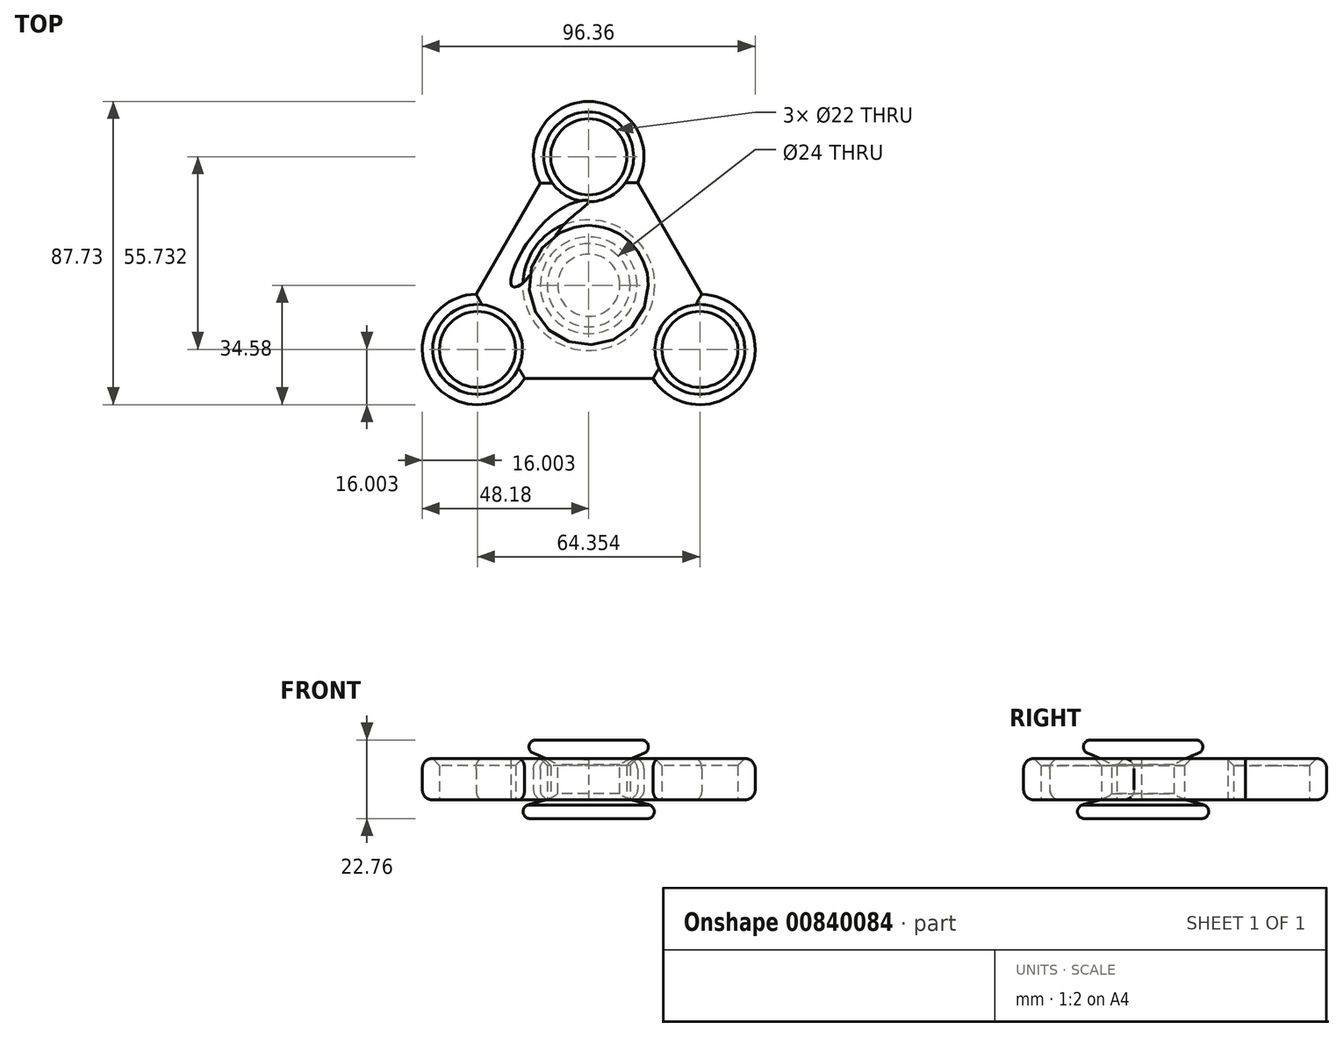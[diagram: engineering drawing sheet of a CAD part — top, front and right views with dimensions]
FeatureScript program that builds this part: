
annotation { "Feature Type Name" : "Feature", "Feature Type Description" : "" }
export const myFeature = defineFeature(function(context is Context, id is Id, definition is map)
    precondition{}
    {
        {
            var Q0;
            Q0=qCreatedBy(makeId("Top.planeOp"),FACE);
            var sketch = newSketch(context, id + "F0", { "sketchPlane" : qUnion([Q0])});
            skCircle(sketch, "E0", {"center": v(0, 37.15) * mm, "radius": 11 * mm});
            skArc(sketch, "E1.0", {"start": v(14.07, 29.53) * mm, "mid": v(0, 53.15) * mm, "end": v(-14.07, 29.53) * mm});
            skArc(sketch, "E2.1.0", {"start": v(-32.61, -2.58) * mm, "mid": v(-46.03, -26.58) * mm, "end": v(-18.54, -26.95) * mm});
            skCircle(sketch, "E2.1.1", {"center": v(-32.18, -18.58) * mm, "radius": 11 * mm});
            skArc(sketch, "E2.2.0", {"start": v(18.54, -26.95) * mm, "mid": v(46.03, -26.58) * mm, "end": v(32.61, -2.58) * mm});
            skCircle(sketch, "E2.2.1", {"center": v(32.18, -18.58) * mm, "radius": 11 * mm});
            skPoint(sketch, "E2.center", {"position": v(0, 0) * mm});
            skCircle(sketch, "E3", {"center": v(0, 0) * mm, "radius": 12 * mm});
            skPoint(sketch, "E4.0.midPoint", {"position": v(-32.71, 0) * mm});
            skArc(sketch, "E5.trimOffspring", {"start": v(18.42, -27.04) * mm, "mid": v(18.48, -27) * mm, "end": v(18.54, -26.95) * mm, "construction": true});
            skPoint(sketch, "E6.orphan", {"position": v(-32.71, -18.89) * mm});
            skPoint(sketch, "E7.orphan", {"position": v(0, 37.77) * mm});
            skArc(sketch, "E8.trimOffspring", {"start": v(14.2, 29.47) * mm, "mid": v(14.14, 29.5) * mm, "end": v(14.07, 29.53) * mm, "construction": true});
            skArc(sketch, "E9.trimOffspring", {"start": v(32.61, -2.58) * mm, "mid": v(32.62, -2.5) * mm, "end": v(32.62, -2.43) * mm, "construction": true});
            skPoint(sketch, "E10.orphan", {"position": v(32.71, -18.89) * mm});
            skPoint(sketch, "E11.visualSharp", {"position": v(-32.71, 18.89) * mm});
            skPoint(sketch, "E12.visualSharp", {"position": v(32.71, 18.89) * mm});
            skPoint(sketch, "E13.visualSharp", {"position": v(0, -37.77) * mm});
            skLineSegment(sketch, "E14", {"start": v(14.12, 29.62) * mm, "end": v(32.71, -2.59) * mm});
            skLineSegment(sketch, "E15", {"start": v(-14.07, 29.53) * mm, "end": v(-32.61, -2.58) * mm});
            skLineSegment(sketch, "E16", {"start": v(-18.54, -26.95) * mm, "end": v(18.6, -27.04) * mm});
            skSolve(sketch);
        }
        {
            var Q0;
            Q0=makeQuery(id+"F0.imprint","IMPRINT",FACE,{"disambiguationData":[TD([[makeQuery(id+"F0.imprint","IMPRINT",EDGE,{"derivedFrom":sQuery(id+"F0.wireOp",EDGE,"E0")}),-1.0]])]});
            extrude(context, id + "F1", {"entities" : qUnion([Q0]), "endBound" : BoundingType.SYMMETRIC, "depth" : 12 * mm, "offsetDistance" : 25 * mm});
        }
        {
            var Q0;
            Q0=makeQuery(id+"F1.opExtrude","CAP_EDGE",EDGE,{"disambiguationData":[OSD([sQuery(id+"F0.wireOp",EDGE,"E4.1")])],"isStart":false});
            var Q1;
            Q1=makeQuery(id+"F1.opExtrude","CAP_EDGE",EDGE,{"disambiguationData":[OSD([sQuery(id+"F0.wireOp",EDGE,"E11.filletArc")])],"isStart":false});
            var Q2;
            Q2=makeQuery(id+"F1.opExtrude","CAP_EDGE",EDGE,{"disambiguationData":[OSD([sQuery(id+"F0.wireOp",EDGE,"E4.0")])],"isStart":false});
            var Q3;
            Q3=makeQuery(id+"F1.opExtrude","CAP_EDGE",EDGE,{"disambiguationData":[OSD([sQuery(id+"F0.wireOp",EDGE,"E2.1.0")])],"isStart":false});
            var Q4;
            Q4=makeQuery(id+"F1.opExtrude","CAP_EDGE",EDGE,{"disambiguationData":[OSD([sQuery(id+"F0.wireOp",EDGE,"E4.5")])],"isStart":false});
            var Q5;
            Q5=makeQuery(id+"F1.opExtrude","CAP_EDGE",EDGE,{"disambiguationData":[OSD([sQuery(id+"F0.wireOp",EDGE,"E4.4")])],"isStart":false});
            var Q6;
            Q6=makeQuery(id+"F1.opExtrude","CAP_EDGE",EDGE,{"disambiguationData":[OSD([sQuery(id+"F0.wireOp",EDGE,"E13.filletArc")])],"isStart":false});
            var Q7;
            Q7=makeQuery(id+"F1.opExtrude","CAP_EDGE",EDGE,{"disambiguationData":[OSD([sQuery(id+"F0.wireOp",EDGE,"E2.2.0")])],"isStart":false});
            var Q8;
            Q8=makeQuery(id+"F1.opExtrude","CAP_EDGE",EDGE,{"disambiguationData":[OSD([sQuery(id+"F0.wireOp",EDGE,"E4.3")])],"isStart":false});
            var Q9;
            Q9=makeQuery(id+"F1.opExtrude","CAP_EDGE",EDGE,{"disambiguationData":[OSD([sQuery(id+"F0.wireOp",EDGE,"E12.filletArc")])],"isStart":false});
            var Q10;
            Q10=makeQuery(id+"F1.opExtrude","CAP_EDGE",EDGE,{"disambiguationData":[OSD([sQuery(id+"F0.wireOp",EDGE,"E4.2")])],"isStart":false});
            var Q11;
            Q11=makeQuery(id+"F1.opExtrude","CAP_EDGE",EDGE,{"disambiguationData":[OSD([sQuery(id+"F0.wireOp",EDGE,"E1.0")])],"isStart":false});
            fillet(context, id + "F2", {"entities" : qUnion([Q0, Q1, Q2, Q3, Q4, Q5, Q6, Q7, Q8, Q9, Q10, Q11]), "radius" : 3 * mm, "tangentPropagation" : true, "allowEdgeOverflow" : false});
        }
        {
            var Q0;
            Q0=makeQuery(id+"F1.opExtrude","CAP_FACE",FACE,{"disambiguationData":[OSD([sQuery(id+"F0.wireOp",EDGE,"E0"),sQuery(id+"F0.wireOp",EDGE,"E1.0"),sQuery(id+"F0.wireOp",EDGE,"E2.1.0"),sQuery(id+"F0.wireOp",EDGE,"E2.1.1"),sQuery(id+"F0.wireOp",EDGE,"E2.2.0"),sQuery(id+"F0.wireOp",EDGE,"E2.2.1"),sQuery(id+"F0.wireOp",EDGE,"E3"),sQuery(id+"F0.wireOp",EDGE,"E4.0"),sQuery(id+"F0.wireOp",EDGE,"E4.1"),sQuery(id+"F0.wireOp",EDGE,"E4.2"),sQuery(id+"F0.wireOp",EDGE,"E4.3"),sQuery(id+"F0.wireOp",EDGE,"E4.4"),sQuery(id+"F0.wireOp",EDGE,"E4.5"),sQuery(id+"F0.wireOp",EDGE,"E11.filletArc"),sQuery(id+"F0.wireOp",EDGE,"E12.filletArc"),sQuery(id+"F0.wireOp",EDGE,"E13.filletArc")])],"isStart":false});
            var sketch = newSketch(context, id + "F3", { "sketchPlane" : qUnion([Q0])});
            skPoint(sketch, "E17.0.internal.snap0", {"position": v(-18.02, 22.93) * mm});
            skPoint(sketch, "E17.7.internal.snap0", {"position": v(-18.02, 24.33) * mm});
            skFitSpline(sketch, "E17", {"points": [v(-6.56, 22.93) * mm, v(-15.86, 14.71) * mm, v(-20.62, 7.32) * mm, v(-22.39, 0) * mm, v(-19.88, 0) * mm, v(-11.64, 11.2) * mm, v(-5.23, 19.44) * mm, v(0, 24.33) * mm, v(-6.56, 22.93) * mm]});
            skSolve(sketch);
        }
        {
            var Q0;
            Q0=makeQuery(id+"F3.imprint","IMPRINT",FACE,{"disambiguationData":[TD([[makeQuery(id+"F3.imprint","IMPRINT",EDGE,{"derivedFrom":sQuery(id+"F3.wireOp",EDGE,"E17")}),1.0]])]});
            extrude(context, id + "F4", {"entities" : qUnion([Q0]), "operationType" : NewBodyOperationType.REMOVE, "endBound" : BoundingType.THROUGH_ALL, "oppositeDirection" : true, "depth" : 7 * mm, "offsetDistance" : 25 * mm});
        }
        {
            var Q0;
            Q0=makeQuery(id+"F1.opExtrude","CAP_EDGE",EDGE,{"disambiguationData":[OSD([sQuery(id+"F0.wireOp",EDGE,"E15")])],"isStart":false});
            var Q1;
            Q1=makeQuery(id+"F1.opExtrude","CAP_EDGE",EDGE,{"disambiguationData":[OSD([sQuery(id+"F0.wireOp",EDGE,"E16")])],"isStart":false});
            var Q2;
            Q2=makeQuery(id+"F1.opExtrude","CAP_EDGE",EDGE,{"disambiguationData":[OSD([sQuery(id+"F0.wireOp",EDGE,"E14")])],"isStart":false});
            fillet(context, id + "F5", {"entities" : qUnion([Q0, Q1, Q2]), "radius" : 3 * mm, "tangentPropagation" : true, "allowEdgeOverflow" : false});
        }
        {
            var Q0;
            Q0=makeQuery(id+"F1.opExtrude","CAP_EDGE",EDGE,{"disambiguationData":[OSD([sQuery(id+"F0.wireOp",EDGE,"E15")])],"isStart":true});
            var Q1;
            Q1=makeQuery(id+"F1.opExtrude","CAP_EDGE",EDGE,{"disambiguationData":[OSD([sQuery(id+"F0.wireOp",EDGE,"E2.1.0")])],"isStart":true});
            var Q2;
            Q2=makeQuery(id+"F1.opExtrude","CAP_EDGE",EDGE,{"disambiguationData":[OSD([sQuery(id+"F0.wireOp",EDGE,"E16")])],"isStart":true});
            var Q3;
            Q3=makeQuery(id+"F1.opExtrude","CAP_EDGE",EDGE,{"disambiguationData":[OSD([sQuery(id+"F0.wireOp",EDGE,"E2.2.0")])],"isStart":true});
            var Q4;
            Q4=makeQuery(id+"F1.opExtrude","CAP_EDGE",EDGE,{"disambiguationData":[OSD([sQuery(id+"F0.wireOp",EDGE,"E14")])],"isStart":true});
            var Q5;
            Q5=makeQuery(id+"F1.opExtrude","CAP_EDGE",EDGE,{"disambiguationData":[OSD([sQuery(id+"F0.wireOp",EDGE,"E1.0")])],"isStart":true});
            fillet(context, id + "F6", {"entities" : qUnion([Q0, Q1, Q2, Q3, Q4, Q5]), "radius" : 3 * mm, "tangentPropagation" : true, "allowEdgeOverflow" : false});
        }
        {
            var Q0;
            Q0=makeQuery(id+"F1.opExtrude","CAP_EDGE",EDGE,{"disambiguationData":[OSD([sQuery(id+"F0.wireOp",EDGE,"E3")])],"isStart":false});
            var Q1;
            Q1=makeQuery(id+"F1.opExtrude","CAP_EDGE",EDGE,{"disambiguationData":[OSD([sQuery(id+"F0.wireOp",EDGE,"E2.2.1")])],"isStart":false});
            var Q2;
            Q2=makeQuery(id+"F1.opExtrude","CAP_EDGE",EDGE,{"disambiguationData":[OSD([sQuery(id+"F0.wireOp",EDGE,"E0")])],"isStart":false});
            var Q3;
            Q3=makeQuery(id+"F1.opExtrude","CAP_EDGE",EDGE,{"disambiguationData":[OSD([sQuery(id+"F0.wireOp",EDGE,"E2.1.1")])],"isStart":false});
            chamfer(context, id + "F7", {"entities" : qUnion([Q0, Q1, Q2, Q3]), "width" : 2 * mm, "tangentPropagation" : true});
        }
        {
            var Q0;
            Q0=qCreatedBy(makeId("Right.planeOp"),FACE);
            var sketch = newSketch(context, id + "F8", { "sketchPlane" : qUnion([Q0])});
            skLineSegment(sketch, "E18", {"start": v(-25, 11.36) * mm, "end": v(0, 11.36) * mm});
            skLineSegment(sketch, "E19", {"start": v(0, 11.36) * mm, "end": v(0, -11.4) * mm});
            skLineSegment(sketch, "E20", {"start": v(0, -11.4) * mm, "end": v(-25, -11.4) * mm});
            skLineSegment(sketch, "E21", {"start": v(-9, 4.17) * mm, "end": v(-9, -4.18) * mm});
            skFitSpline(sketch, "E22", {"points": [v(-25, 11.36) * mm, v(-17.64, 8.13) * mm, v(-9, 4.17) * mm], "startDerivative": vector(9.17, -5.68) * mm, "endDerivative": vector(12.64, -8.59) * mm});
            skFitSpline(sketch, "E23", {"points": [v(-25, -11.4) * mm, v(-17.73, -7.53) * mm, v(-9, -4.18) * mm], "startDerivative": vector(11.42, 3.22) * mm, "endDerivative": vector(10.55, 11) * mm});
            skSolve(sketch);
        }
        {
            var Q0;
            Q0=makeQuery(id+"F8.imprint","IMPRINT",FACE,{"disambiguationData":[TD([[makeQuery(id+"F8.imprint","IMPRINT",EDGE,{"derivedFrom":sQuery(id+"F8.wireOp",EDGE,"E18")}),-1.0]])]});
            var Q1;
            Q1=sQuery(id+"F8.wireOp",EDGE,"E19");
            revolve(context, id + "F9", {"surfaceOperationType" : NewSurfaceOperationType.NEW, "entities" : qUnion([Q0]), "axis" : qUnion([Q1]), "revolveType" : RevolveType.FULL});
        }
        {
            var Q0;
            Q0=makeQuery(id+"F9.opRevolve","SWEPT_EDGE",EDGE,{"disambiguationData":[OSD([sQuery(id+"F8.wireOp",EDGE,"E18"),sQuery(id+"F8.wireOp",EDGE,"pPxb5wou-VZB8-x4Uv-9zah-azZgOreIM6fP")])]});
            fillet(context, id + "F10", {"entities" : qUnion([Q0]), "radius" : 2 * mm, "tangentPropagation" : true, "allowEdgeOverflow" : false});
        }
        {
            var Q0;
            Q0=makeQuery(id+"F9.opRevolve","SWEPT_EDGE",EDGE,{"disambiguationData":[OSD([sQuery(id+"F8.wireOp",EDGE,"E20"),sQuery(id+"F8.wireOp",EDGE,"3goSOWTS-yiCJ-8PXl-JM3G-QyR6yf7YQlBz")])]});
            fillet(context, id + "F11", {"entities" : qUnion([Q0]), "radius" : 2 * mm, "tangentPropagation" : true, "allowEdgeOverflow" : false});
        }
    });
